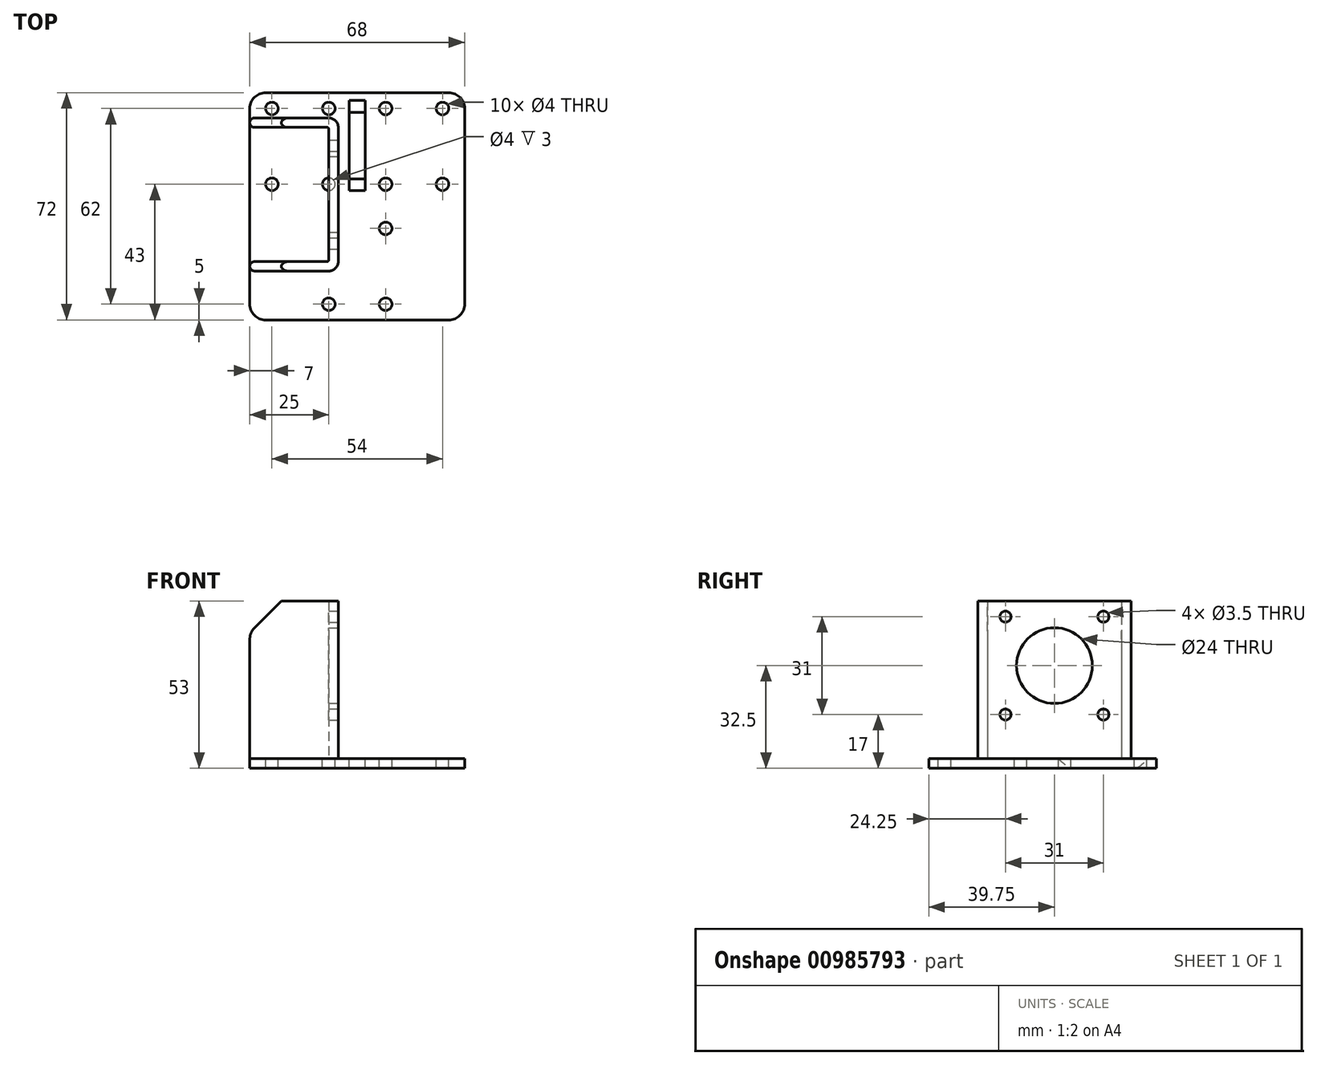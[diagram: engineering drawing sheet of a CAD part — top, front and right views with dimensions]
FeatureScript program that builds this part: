
annotation { "Feature Type Name" : "Feature", "Feature Type Description" : "" }
export const myFeature = defineFeature(function(context is Context, id is Id, definition is map)
    precondition{}
    {
        {
            var Q0;
            Q0=qCreatedBy(makeId("Top.planeOp"),FACE);
            var sketch = newSketch(context, id + "F0", { "sketchPlane" : qUnion([Q0])});
            skLineSegment(sketch, "E0.bottom", {"start": v(34, 0) * mm, "end": v(-34, 0) * mm});
            skLineSegment(sketch, "E0.top", {"start": v(34, 72) * mm, "end": v(-34, 72) * mm});
            skLineSegment(sketch, "E0.left", {"start": v(34, 0) * mm, "end": v(34, 72) * mm});
            skLineSegment(sketch, "E0.right", {"start": v(-34, 0) * mm, "end": v(-34, 72) * mm});
            skCircle(sketch, "E1", {"center": v(27, 67) * mm, "radius": 2 * mm});
            skCircle(sketch, "E2", {"center": v(27, 43) * mm, "radius": 2 * mm});
            skCircle(sketch, "E3", {"center": v(9, 67) * mm, "radius": 2 * mm});
            skCircle(sketch, "E4", {"center": v(9, 43) * mm, "radius": 2 * mm});
            skLineSegment(sketch, "E5", {"start": v(0, 72) * mm, "end": v(0, -67.13) * mm, "construction": true});
            skCircle(sketch, "E6.MirrorC", {"center": v(-27, 67) * mm, "radius": 2 * mm});
            skCircle(sketch, "E7.MirrorC", {"center": v(-27, 43) * mm, "radius": 2 * mm});
            skCircle(sketch, "E8.MirrorC", {"center": v(-9, 43) * mm, "radius": 2 * mm});
            skCircle(sketch, "E9.MirrorC", {"center": v(-9, 67) * mm, "radius": 2 * mm});
            skLineSegment(sketch, "E10", {"start": v(34, 36) * mm, "end": v(-10.03, 36) * mm, "construction": true});
            skCircle(sketch, "E11.MirrorC", {"center": v(9, 29) * mm, "radius": 2 * mm});
            skCircle(sketch, "E12.MirrorC", {"center": v(-9, 29) * mm, "radius": 2 * mm});
            skCircle(sketch, "E13.MirrorC", {"center": v(-9, 5) * mm, "radius": 2 * mm});
            skCircle(sketch, "E14.MirrorC", {"center": v(9, 5) * mm, "radius": 2 * mm});
            skLineSegment(sketch, "E15.bottom", {"start": v(3, 72) * mm, "end": v(33, 72) * mm, "construction": true});
            skLineSegment(sketch, "E15.top", {"start": v(3, 38) * mm, "end": v(33, 38) * mm, "construction": true});
            skLineSegment(sketch, "E15.left", {"start": v(3, 72) * mm, "end": v(3, 38) * mm, "construction": true});
            skLineSegment(sketch, "E15.right", {"start": v(33, 72) * mm, "end": v(33, 38) * mm, "construction": true});
            skLineSegment(sketch, "E16.bottom", {"start": v(15, 34) * mm, "end": v(-15, 34) * mm, "construction": true});
            skLineSegment(sketch, "E16.top", {"start": v(15, 0) * mm, "end": v(-15, 0) * mm, "construction": true});
            skLineSegment(sketch, "E16.left", {"start": v(15, 34) * mm, "end": v(15, 0) * mm, "construction": true});
            skLineSegment(sketch, "E16.right", {"start": v(-15, 34) * mm, "end": v(-15, 0) * mm, "construction": true});
            skLineSegment(sketch, "E17.MirrorCS", {"start": v(-3, 72) * mm, "end": v(-3, 38) * mm, "construction": true});
            skLineSegment(sketch, "E18.MirrorCS", {"start": v(-3, 38) * mm, "end": v(-33, 38) * mm, "construction": true});
            skLineSegment(sketch, "E19.MirrorCS", {"start": v(-33, 72) * mm, "end": v(-33, 38) * mm, "construction": true});
            skPoint(sketch, "E20", {"position": v(0, 0) * mm});
            skSolve(sketch);
        }
        {
            var Q0;
            Q0=makeQuery(id+"F0.imprint","IMPRINT",FACE,{"disambiguationData":[TD([[makeQuery(id+"F0.imprint","IMPRINT",EDGE,{"derivedFrom":sQuery(id+"F0.wireOp",EDGE,"E0.bottom")}),-1.0]])]});
            var Q1;
            Q1=makeQuery(id+"F0.imprint","IMPRINT",FACE,{"disambiguationData":[TD([[makeQuery(id+"F0.imprint","IMPRINT",EDGE,{"derivedFrom":sQuery(id+"F0.wireOp",EDGE,"E8.MirrorC")}),-1.0]])]});
            var Q2;
            Q2=makeQuery(id+"F0.imprint","IMPRINT",FACE,{"disambiguationData":[TD([[makeQuery(id+"F0.imprint","IMPRINT",EDGE,{"derivedFrom":sQuery(id+"F0.wireOp",EDGE,"E12.MirrorC")}),1.0]])]});
            extrude(context, id + "F1", {"entities" : qUnion([Q0, Q1, Q2]), "oppositeDirection" : true, "depth" : 3 * mm, "offsetDistance" : 25 * mm});
        }
        {
            var Q0;
            Q0=qCreatedBy(makeId("Top.planeOp"),FACE);
            var sketch = newSketch(context, id + "F2", { "sketchPlane" : qUnion([Q0])});
            skLineSegment(sketch, "E21.0", {"start": v(34, 72) * mm, "end": v(-34, 72) * mm});
            skLineSegment(sketch, "E22.0", {"start": v(34, 0) * mm, "end": v(34, 72) * mm});
            skLineSegment(sketch, "E23.0", {"start": v(34, 0) * mm, "end": v(-34, 0) * mm});
            skLineSegment(sketch, "E24.0", {"start": v(-34, 0) * mm, "end": v(-34, 72) * mm});
            skLineSegment(sketch, "E25", {"start": v(-34, 64) * mm, "end": v(-6, 64) * mm});
            skLineSegment(sketch, "E26", {"start": v(-6, 64) * mm, "end": v(-6, 15.5) * mm});
            skLineSegment(sketch, "E27", {"start": v(-6, 15.5) * mm, "end": v(-34, 15.5) * mm});
            skPoint(sketch, "E28", {"position": v(-6, 39.75) * mm});
            skPoint(sketch, "E29", {"position": v(-34, 36) * mm});
            skLineSegment(sketch, "E30.0", {"start": v(-9, 18.5) * mm, "end": v(-34, 18.5) * mm});
            skLineSegment(sketch, "E30.1", {"start": v(-9, 61) * mm, "end": v(-9, 18.5) * mm});
            skLineSegment(sketch, "E30.2", {"start": v(-34, 61) * mm, "end": v(-9, 61) * mm});
            skSolve(sketch);
        }
        {
            var Q0;
            {var subQ0=sQuery(id+"F2.wireOp",EDGE,"E25");Q0=makeQuery(id+"F2.imprint","IMPRINT",FACE,{"disambiguationData":[TD([[makeQuery(id+"F2.imprint","IMPRINT",EDGE,{"derivedFrom":subQ0}),-1.0]])]});}
            extrude(context, id + "F3", {"entities" : qUnion([Q0]), "operationType" : NewBodyOperationType.ADD, "depth" : 50 * mm, "offsetDistance" : 25 * mm});
        }
        {
            var Q0;
            {var subQ0=sQuery(id+"F2.wireOp",EDGE,"E24.0");Q0=makeQuery(id+"F3.opExtrude","CAP_EDGE",EDGE,{"disambiguationData":[OSD([subQ0]),TDD([makeQuery(id+"F2.imprint","IMPRINT",EDGE,{"disambiguationData":[TD([[makeQuery(id+"F2.imprint","INTERSECT",VERTEX,{"derivedFrom":[subQ0,sQuery(id+"F2.wireOp",EDGE,"E25")]}),1.0]])],"derivedFrom":subQ0})])],"isStart":false});}
            var Q1;
            {var subQ0=sQuery(id+"F2.wireOp",EDGE,"E24.0");Q1=makeQuery(id+"F3.opExtrude","CAP_EDGE",EDGE,{"disambiguationData":[OSD([subQ0]),TDD([makeQuery(id+"F2.imprint","IMPRINT",EDGE,{"disambiguationData":[TD([[makeQuery(id+"F2.imprint","INTERSECT",VERTEX,{"derivedFrom":[subQ0,sQuery(id+"F2.wireOp",EDGE,"E27")]}),-1.0]])],"derivedFrom":subQ0})])],"isStart":false});}
            chamfer(context, id + "F4", {"entities" : qUnion([Q0, Q1]), "width" : 10 * mm, "tangentPropagation" : true});
        }
        {
            var Q0;
            Q0=makeQuery(id+"F3.opExtrude","SWEPT_FACE",FACE,{"disambiguationData":[OSD([sQuery(id+"F2.wireOp",EDGE,"E26")])]});
            var sketch = newSketch(context, id + "F5", { "sketchPlane" : qUnion([Q0])});
            skPoint(sketch, "E31", {"position": v(74.45, 33.02) * mm});
            skPoint(sketch, "E32", {"position": v(29.84, 9.87) * mm});
            skSolve(sketch);
        }
        {
            var Q0;
            {var subQ0=sQuery(id+"F2.wireOp",EDGE,"E26");Q0=makeQuery(id+"F5.imprint","IMPRINT",FACE,{"disambiguationData":[TD([[makeQuery(id+"F5.imprint","IMPRINT",EDGE,{"derivedFrom":makeQuery(id+"F3.opExtrude","CAP_EDGE",EDGE,{"disambiguationData":[OSD([subQ0])],"isStart":false})}),1.0]])]});}
            var sketch = newSketch(context, id + "F6", { "sketchPlane" : qUnion([Q0])});
            skLineSegment(sketch, "E33.0.0", {"start": v(15.5, 0) * mm, "end": v(64, 0) * mm});
            skLineSegment(sketch, "E33.0.1", {"start": v(64, 0) * mm, "end": v(64, 50) * mm});
            skLineSegment(sketch, "E33.0.2", {"start": v(64, 50) * mm, "end": v(15.5, 50) * mm});
            skLineSegment(sketch, "E33.0.3", {"start": v(15.5, 50) * mm, "end": v(15.5, 0) * mm});
            skLineSegment(sketch, "E34", {"start": v(64, 50) * mm, "end": v(15.5, 0) * mm, "construction": true});
            skPoint(sketch, "E35", {"position": v(39.75, 25) * mm});
            skCircle(sketch, "E36", {"center": v(55.25, 45) * mm, "radius": 1.75 * mm});
            skCircle(sketch, "E37", {"center": v(55.25, 14) * mm, "radius": 1.75 * mm});
            skCircle(sketch, "E38", {"center": v(24.25, 45) * mm, "radius": 1.75 * mm});
            skCircle(sketch, "E39", {"center": v(24.25, 14) * mm, "radius": 1.75 * mm});
            skCircle(sketch, "E40", {"center": v(39.75, 29.5) * mm, "radius": 12 * mm});
            skSolve(sketch);
        }
        {
            var Q0;
            Q0=makeQuery(id+"F6.imprint","IMPRINT",FACE,{"disambiguationData":[TD([[makeQuery(id+"F6.imprint","IMPRINT",EDGE,{"derivedFrom":sQuery(id+"F6.wireOp",EDGE,"E36")}),1.0]])]});
            var Q1;
            Q1=makeQuery(id+"F6.imprint","IMPRINT",FACE,{"disambiguationData":[TD([[makeQuery(id+"F6.imprint","IMPRINT",EDGE,{"derivedFrom":sQuery(id+"F6.wireOp",EDGE,"E40")}),1.0]])]});
            var Q2;
            Q2=makeQuery(id+"F6.imprint","IMPRINT",FACE,{"disambiguationData":[TD([[makeQuery(id+"F6.imprint","IMPRINT",EDGE,{"derivedFrom":sQuery(id+"F6.wireOp",EDGE,"E37")}),1.0]])]});
            var Q3;
            Q3=makeQuery(id+"F6.imprint","IMPRINT",FACE,{"disambiguationData":[TD([[makeQuery(id+"F6.imprint","IMPRINT",EDGE,{"derivedFrom":sQuery(id+"F6.wireOp",EDGE,"E38")}),1.0]])]});
            var Q4;
            Q4=makeQuery(id+"F6.imprint","IMPRINT",FACE,{"disambiguationData":[TD([[makeQuery(id+"F6.imprint","IMPRINT",EDGE,{"derivedFrom":sQuery(id+"F6.wireOp",EDGE,"E39")}),1.0]])]});
            extrude(context, id + "F7", {"entities" : qUnion([Q0, Q1, Q2, Q3, Q4]), "operationType" : NewBodyOperationType.REMOVE, "oppositeDirection" : true, "depth" : 25 * mm, "offsetDistance" : 25 * mm});
        }
        {
            var Q0;
            Q0=makeQuery(id+"F1.opExtrude","SWEPT_EDGE",EDGE,{"disambiguationData":[OSD([sQuery(id+"F0.wireOp",EDGE,"E0.top"),sQuery(id+"F0.wireOp",EDGE,"E0.right")])]});
            var Q1;
            Q1=makeQuery(id+"F1.opExtrude","SWEPT_EDGE",EDGE,{"disambiguationData":[OSD([sQuery(id+"F0.wireOp",EDGE,"E0.top"),sQuery(id+"F0.wireOp",EDGE,"E0.left")])]});
            var Q2;
            Q2=makeQuery(id+"F1.opExtrude","SWEPT_EDGE",EDGE,{"disambiguationData":[OSD([sQuery(id+"F0.wireOp",EDGE,"E0.bottom"),sQuery(id+"F0.wireOp",EDGE,"E0.left")])]});
            var Q3;
            Q3=makeQuery(id+"F1.opExtrude","SWEPT_EDGE",EDGE,{"disambiguationData":[OSD([sQuery(id+"F0.wireOp",EDGE,"E0.bottom"),sQuery(id+"F0.wireOp",EDGE,"E0.right")])]});
            var Q4;
            {var subQ0=sQuery(id+"F2.wireOp",EDGE,"E24.0");var subQ1=makeQuery(id+"F2.imprint","IMPRINT",EDGE,{"disambiguationData":[TD([[makeQuery(id+"F2.imprint","INTERSECT",VERTEX,{"derivedFrom":[subQ0,sQuery(id+"F2.wireOp",EDGE,"E30.0")]}),1.0]])],"derivedFrom":subQ0});Q4=makeQuery(id+"F4.opChamfer","BLEND_EDGE",EDGE,{"blendedFrom":[makeQuery(id+"F3.opExtrude","CAP_EDGE",EDGE,{"disambiguationData":[OSD([subQ0]),TDD([subQ1])],"isStart":false}),makeQuery(id+"F3.boolean.opBoolean","MERGE",FACE,{"derivedFrom":[makeQuery(id+"F1.opExtrude","SWEPT_FACE",FACE,{"disambiguationData":[OSD([sQuery(id+"F0.wireOp",EDGE,"E0.right")])]}),makeQuery(id+"F3.opExtrude","SWEPT_FACE",FACE,{"disambiguationData":[OSD([subQ0]),TDD([makeQuery(id+"F2.imprint","IMPRINT",EDGE,{"disambiguationData":[TD([[makeQuery(id+"F2.imprint","INTERSECT",VERTEX,{"derivedFrom":[subQ0,sQuery(id+"F2.wireOp",EDGE,"E25")]}),1.0]])],"derivedFrom":subQ0})])]}),makeQuery(id+"F3.opExtrude","SWEPT_FACE",FACE,{"disambiguationData":[OSD([subQ0]),TDD([subQ1])]})]})],"blendedInto":[makeQuery(id+"F3.boolean.opBoolean","MERGE",FACE,{"derivedFrom":[makeQuery(id+"F1.opExtrude","SWEPT_FACE",FACE,{"disambiguationData":[OSD([sQuery(id+"F0.wireOp",EDGE,"E0.right")])]}),makeQuery(id+"F3.opExtrude","SWEPT_FACE",FACE,{"disambiguationData":[OSD([subQ0]),TDD([makeQuery(id+"F2.imprint","IMPRINT",EDGE,{"disambiguationData":[TD([[makeQuery(id+"F2.imprint","INTERSECT",VERTEX,{"derivedFrom":[subQ0,sQuery(id+"F2.wireOp",EDGE,"E25")]}),1.0]])],"derivedFrom":subQ0})])]}),makeQuery(id+"F3.opExtrude","SWEPT_FACE",FACE,{"disambiguationData":[OSD([subQ0]),TDD([subQ1])]})]})]});}
            var Q5;
            {var subQ0=sQuery(id+"F2.wireOp",EDGE,"E24.0");var subQ1=makeQuery(id+"F2.imprint","IMPRINT",EDGE,{"disambiguationData":[TD([[makeQuery(id+"F2.imprint","INTERSECT",VERTEX,{"derivedFrom":[subQ0,sQuery(id+"F2.wireOp",EDGE,"E25")]}),1.0]])],"derivedFrom":subQ0});Q5=makeQuery(id+"F4.opChamfer","BLEND_EDGE",EDGE,{"blendedFrom":[makeQuery(id+"F3.opExtrude","CAP_EDGE",EDGE,{"disambiguationData":[OSD([subQ0]),TDD([subQ1])],"isStart":false}),makeQuery(id+"F3.boolean.opBoolean","MERGE",FACE,{"derivedFrom":[makeQuery(id+"F1.opExtrude","SWEPT_FACE",FACE,{"disambiguationData":[OSD([sQuery(id+"F0.wireOp",EDGE,"E0.right")])]}),makeQuery(id+"F3.opExtrude","SWEPT_FACE",FACE,{"disambiguationData":[OSD([subQ0]),TDD([subQ1])]}),makeQuery(id+"F3.opExtrude","SWEPT_FACE",FACE,{"disambiguationData":[OSD([subQ0]),TDD([makeQuery(id+"F2.imprint","IMPRINT",EDGE,{"disambiguationData":[TD([[makeQuery(id+"F2.imprint","INTERSECT",VERTEX,{"derivedFrom":[subQ0,sQuery(id+"F2.wireOp",EDGE,"E30.0")]}),1.0]])],"derivedFrom":subQ0})])]})]})],"blendedInto":[makeQuery(id+"F3.boolean.opBoolean","MERGE",FACE,{"derivedFrom":[makeQuery(id+"F1.opExtrude","SWEPT_FACE",FACE,{"disambiguationData":[OSD([sQuery(id+"F0.wireOp",EDGE,"E0.right")])]}),makeQuery(id+"F3.opExtrude","SWEPT_FACE",FACE,{"disambiguationData":[OSD([subQ0]),TDD([subQ1])]}),makeQuery(id+"F3.opExtrude","SWEPT_FACE",FACE,{"disambiguationData":[OSD([subQ0]),TDD([makeQuery(id+"F2.imprint","IMPRINT",EDGE,{"disambiguationData":[TD([[makeQuery(id+"F2.imprint","INTERSECT",VERTEX,{"derivedFrom":[subQ0,sQuery(id+"F2.wireOp",EDGE,"E30.0")]}),1.0]])],"derivedFrom":subQ0})])]})]})]});}
            fillet(context, id + "F8", {"entities" : qUnion([Q0, Q1, Q2, Q3, Q4, Q5]), "tangentPropagation" : true, "radius" : 5 * mm, "defaultsChanged" : true, "vertexSettings" : [], "allowEdgeOverflow" : false});
        }
        {
            var Q0;
            Q0=makeQuery(id+"F3.opExtrude","SWEPT_EDGE",EDGE,{"disambiguationData":[OSD([sQuery(id+"F2.wireOp",EDGE,"E24.0"),sQuery(id+"F2.wireOp",EDGE,"E25")])]});
            var Q1;
            Q1=makeQuery(id+"F3.opExtrude","SWEPT_EDGE",EDGE,{"disambiguationData":[OSD([sQuery(id+"F2.wireOp",EDGE,"E24.0"),sQuery(id+"F2.wireOp",EDGE,"E30.2")])]});
            var Q2;
            {var subQ0=sQuery(id+"F2.wireOp",EDGE,"E27");var subQ1=sQuery(id+"F2.wireOp",EDGE,"E24.0");Q2=makeQuery(id+"F4.opChamfer","BLEND_EDGE",EDGE,{"blendedFrom":[makeQuery(id+"F3.opExtrude","CAP_EDGE",EDGE,{"disambiguationData":[OSD([subQ1]),TDD([makeQuery(id+"F2.imprint","IMPRINT",EDGE,{"disambiguationData":[TD([[makeQuery(id+"F2.imprint","INTERSECT",VERTEX,{"derivedFrom":[subQ1,sQuery(id+"F2.wireOp",EDGE,"E30.0")]}),1.0]])],"derivedFrom":subQ1})])],"isStart":false}),makeQuery(id+"F3.opExtrude","SWEPT_FACE",FACE,{"disambiguationData":[OSD([subQ0])]})],"blendedInto":[makeQuery(id+"F3.opExtrude","SWEPT_FACE",FACE,{"disambiguationData":[OSD([subQ0])]})]});}
            var Q3;
            {var subQ0=sQuery(id+"F2.wireOp",EDGE,"E30.0");var subQ1=sQuery(id+"F2.wireOp",EDGE,"E24.0");Q3=makeQuery(id+"F4.opChamfer","BLEND_EDGE",EDGE,{"blendedFrom":[makeQuery(id+"F3.opExtrude","CAP_EDGE",EDGE,{"disambiguationData":[OSD([subQ1]),TDD([makeQuery(id+"F2.imprint","IMPRINT",EDGE,{"disambiguationData":[TD([[makeQuery(id+"F2.imprint","INTERSECT",VERTEX,{"derivedFrom":[subQ1,subQ0]}),1.0]])],"derivedFrom":subQ1})])],"isStart":false}),makeQuery(id+"F3.opExtrude","SWEPT_FACE",FACE,{"disambiguationData":[OSD([subQ0])]})],"blendedInto":[makeQuery(id+"F3.opExtrude","SWEPT_FACE",FACE,{"disambiguationData":[OSD([subQ0])]})]});}
            var Q4;
            {var subQ0=sQuery(id+"F2.wireOp",EDGE,"E27");var subQ1=sQuery(id+"F2.wireOp",EDGE,"E24.0");var subQ2=makeQuery(id+"F2.imprint","IMPRINT",EDGE,{"disambiguationData":[TD([[makeQuery(id+"F2.imprint","INTERSECT",VERTEX,{"derivedFrom":[subQ1,sQuery(id+"F2.wireOp",EDGE,"E30.0")]}),1.0]])],"derivedFrom":subQ1});Q4=makeQuery(id+"F8.opFillet","BLEND_EDGE",EDGE,{"blendedFrom":[makeQuery(id+"F4.opChamfer","BLEND_EDGE",EDGE,{"blendedFrom":[makeQuery(id+"F3.opExtrude","CAP_EDGE",EDGE,{"disambiguationData":[OSD([subQ1]),TDD([subQ2])],"isStart":false}),makeQuery(id+"F3.boolean.opBoolean","MERGE",FACE,{"derivedFrom":[makeQuery(id+"F1.opExtrude","SWEPT_FACE",FACE,{"disambiguationData":[OSD([sQuery(id+"F0.wireOp",EDGE,"E0.right")])]}),makeQuery(id+"F3.opExtrude","SWEPT_FACE",FACE,{"disambiguationData":[OSD([subQ1]),TDD([makeQuery(id+"F2.imprint","IMPRINT",EDGE,{"disambiguationData":[TD([[makeQuery(id+"F2.imprint","INTERSECT",VERTEX,{"derivedFrom":[subQ1,sQuery(id+"F2.wireOp",EDGE,"E25")]}),1.0]])],"derivedFrom":subQ1})])]}),makeQuery(id+"F3.opExtrude","SWEPT_FACE",FACE,{"disambiguationData":[OSD([subQ1]),TDD([subQ2])]})]})],"blendedInto":[makeQuery(id+"F3.boolean.opBoolean","MERGE",FACE,{"derivedFrom":[makeQuery(id+"F1.opExtrude","SWEPT_FACE",FACE,{"disambiguationData":[OSD([sQuery(id+"F0.wireOp",EDGE,"E0.right")])]}),makeQuery(id+"F3.opExtrude","SWEPT_FACE",FACE,{"disambiguationData":[OSD([subQ1]),TDD([makeQuery(id+"F2.imprint","IMPRINT",EDGE,{"disambiguationData":[TD([[makeQuery(id+"F2.imprint","INTERSECT",VERTEX,{"derivedFrom":[subQ1,sQuery(id+"F2.wireOp",EDGE,"E25")]}),1.0]])],"derivedFrom":subQ1})])]}),makeQuery(id+"F3.opExtrude","SWEPT_FACE",FACE,{"disambiguationData":[OSD([subQ1]),TDD([subQ2])]})]})]}),makeQuery(id+"F3.opExtrude","SWEPT_FACE",FACE,{"disambiguationData":[OSD([subQ0])]})],"blendedInto":[makeQuery(id+"F3.opExtrude","SWEPT_FACE",FACE,{"disambiguationData":[OSD([subQ0])]})]});}
            var Q5;
            Q5=makeQuery(id+"F3.opExtrude","SWEPT_EDGE",EDGE,{"disambiguationData":[OSD([sQuery(id+"F2.wireOp",EDGE,"E24.0"),sQuery(id+"F2.wireOp",EDGE,"E27")])]});
            var Q6;
            Q6=makeQuery(id+"F3.opExtrude","SWEPT_EDGE",EDGE,{"disambiguationData":[OSD([sQuery(id+"F2.wireOp",EDGE,"E24.0"),sQuery(id+"F2.wireOp",EDGE,"E30.0")])]});
            var Q7;
            {var subQ0=sQuery(id+"F2.wireOp",EDGE,"E30.0");var subQ1=sQuery(id+"F2.wireOp",EDGE,"E24.0");var subQ2=makeQuery(id+"F2.imprint","IMPRINT",EDGE,{"disambiguationData":[TD([[makeQuery(id+"F2.imprint","INTERSECT",VERTEX,{"derivedFrom":[subQ1,subQ0]}),1.0]])],"derivedFrom":subQ1});Q7=makeQuery(id+"F8.opFillet","BLEND_EDGE",EDGE,{"blendedFrom":[makeQuery(id+"F4.opChamfer","BLEND_EDGE",EDGE,{"blendedFrom":[makeQuery(id+"F3.opExtrude","CAP_EDGE",EDGE,{"disambiguationData":[OSD([subQ1]),TDD([subQ2])],"isStart":false}),makeQuery(id+"F3.boolean.opBoolean","MERGE",FACE,{"derivedFrom":[makeQuery(id+"F1.opExtrude","SWEPT_FACE",FACE,{"disambiguationData":[OSD([sQuery(id+"F0.wireOp",EDGE,"E0.right")])]}),makeQuery(id+"F3.opExtrude","SWEPT_FACE",FACE,{"disambiguationData":[OSD([subQ1]),TDD([makeQuery(id+"F2.imprint","IMPRINT",EDGE,{"disambiguationData":[TD([[makeQuery(id+"F2.imprint","INTERSECT",VERTEX,{"derivedFrom":[subQ1,sQuery(id+"F2.wireOp",EDGE,"E25")]}),1.0]])],"derivedFrom":subQ1})])]}),makeQuery(id+"F3.opExtrude","SWEPT_FACE",FACE,{"disambiguationData":[OSD([subQ1]),TDD([subQ2])]})]})],"blendedInto":[makeQuery(id+"F3.boolean.opBoolean","MERGE",FACE,{"derivedFrom":[makeQuery(id+"F1.opExtrude","SWEPT_FACE",FACE,{"disambiguationData":[OSD([sQuery(id+"F0.wireOp",EDGE,"E0.right")])]}),makeQuery(id+"F3.opExtrude","SWEPT_FACE",FACE,{"disambiguationData":[OSD([subQ1]),TDD([makeQuery(id+"F2.imprint","IMPRINT",EDGE,{"disambiguationData":[TD([[makeQuery(id+"F2.imprint","INTERSECT",VERTEX,{"derivedFrom":[subQ1,sQuery(id+"F2.wireOp",EDGE,"E25")]}),1.0]])],"derivedFrom":subQ1})])]}),makeQuery(id+"F3.opExtrude","SWEPT_FACE",FACE,{"disambiguationData":[OSD([subQ1]),TDD([subQ2])]})]})]}),makeQuery(id+"F3.opExtrude","SWEPT_FACE",FACE,{"disambiguationData":[OSD([subQ0])]})],"blendedInto":[makeQuery(id+"F3.opExtrude","SWEPT_FACE",FACE,{"disambiguationData":[OSD([subQ0])]})]});}
            var Q8;
            {var subQ0=sQuery(id+"F2.wireOp",EDGE,"E25");var subQ1=sQuery(id+"F2.wireOp",EDGE,"E24.0");var subQ2=makeQuery(id+"F2.imprint","IMPRINT",EDGE,{"disambiguationData":[TD([[makeQuery(id+"F2.imprint","INTERSECT",VERTEX,{"derivedFrom":[subQ1,subQ0]}),1.0]])],"derivedFrom":subQ1});Q8=makeQuery(id+"F8.opFillet","BLEND_EDGE",EDGE,{"blendedFrom":[makeQuery(id+"F4.opChamfer","BLEND_EDGE",EDGE,{"blendedFrom":[makeQuery(id+"F3.opExtrude","CAP_EDGE",EDGE,{"disambiguationData":[OSD([subQ1]),TDD([subQ2])],"isStart":false}),makeQuery(id+"F3.boolean.opBoolean","MERGE",FACE,{"derivedFrom":[makeQuery(id+"F1.opExtrude","SWEPT_FACE",FACE,{"disambiguationData":[OSD([sQuery(id+"F0.wireOp",EDGE,"E0.right")])]}),makeQuery(id+"F3.opExtrude","SWEPT_FACE",FACE,{"disambiguationData":[OSD([subQ1]),TDD([subQ2])]}),makeQuery(id+"F3.opExtrude","SWEPT_FACE",FACE,{"disambiguationData":[OSD([subQ1]),TDD([makeQuery(id+"F2.imprint","IMPRINT",EDGE,{"disambiguationData":[TD([[makeQuery(id+"F2.imprint","INTERSECT",VERTEX,{"derivedFrom":[subQ1,sQuery(id+"F2.wireOp",EDGE,"E30.0")]}),1.0]])],"derivedFrom":subQ1})])]})]})],"blendedInto":[makeQuery(id+"F3.boolean.opBoolean","MERGE",FACE,{"derivedFrom":[makeQuery(id+"F1.opExtrude","SWEPT_FACE",FACE,{"disambiguationData":[OSD([sQuery(id+"F0.wireOp",EDGE,"E0.right")])]}),makeQuery(id+"F3.opExtrude","SWEPT_FACE",FACE,{"disambiguationData":[OSD([subQ1]),TDD([subQ2])]}),makeQuery(id+"F3.opExtrude","SWEPT_FACE",FACE,{"disambiguationData":[OSD([subQ1]),TDD([makeQuery(id+"F2.imprint","IMPRINT",EDGE,{"disambiguationData":[TD([[makeQuery(id+"F2.imprint","INTERSECT",VERTEX,{"derivedFrom":[subQ1,sQuery(id+"F2.wireOp",EDGE,"E30.0")]}),1.0]])],"derivedFrom":subQ1})])]})]})]}),makeQuery(id+"F3.opExtrude","SWEPT_FACE",FACE,{"disambiguationData":[OSD([subQ0])]})],"blendedInto":[makeQuery(id+"F3.opExtrude","SWEPT_FACE",FACE,{"disambiguationData":[OSD([subQ0])]})]});}
            var Q9;
            {var subQ0=sQuery(id+"F2.wireOp",EDGE,"E30.2");var subQ1=sQuery(id+"F2.wireOp",EDGE,"E24.0");var subQ2=makeQuery(id+"F2.imprint","IMPRINT",EDGE,{"disambiguationData":[TD([[makeQuery(id+"F2.imprint","INTERSECT",VERTEX,{"derivedFrom":[subQ1,sQuery(id+"F2.wireOp",EDGE,"E25")]}),1.0]])],"derivedFrom":subQ1});Q9=makeQuery(id+"F8.opFillet","BLEND_EDGE",EDGE,{"blendedFrom":[makeQuery(id+"F4.opChamfer","BLEND_EDGE",EDGE,{"blendedFrom":[makeQuery(id+"F3.opExtrude","CAP_EDGE",EDGE,{"disambiguationData":[OSD([subQ1]),TDD([subQ2])],"isStart":false}),makeQuery(id+"F3.boolean.opBoolean","MERGE",FACE,{"derivedFrom":[makeQuery(id+"F1.opExtrude","SWEPT_FACE",FACE,{"disambiguationData":[OSD([sQuery(id+"F0.wireOp",EDGE,"E0.right")])]}),makeQuery(id+"F3.opExtrude","SWEPT_FACE",FACE,{"disambiguationData":[OSD([subQ1]),TDD([subQ2])]}),makeQuery(id+"F3.opExtrude","SWEPT_FACE",FACE,{"disambiguationData":[OSD([subQ1]),TDD([makeQuery(id+"F2.imprint","IMPRINT",EDGE,{"disambiguationData":[TD([[makeQuery(id+"F2.imprint","INTERSECT",VERTEX,{"derivedFrom":[subQ1,sQuery(id+"F2.wireOp",EDGE,"E30.0")]}),1.0]])],"derivedFrom":subQ1})])]})]})],"blendedInto":[makeQuery(id+"F3.boolean.opBoolean","MERGE",FACE,{"derivedFrom":[makeQuery(id+"F1.opExtrude","SWEPT_FACE",FACE,{"disambiguationData":[OSD([sQuery(id+"F0.wireOp",EDGE,"E0.right")])]}),makeQuery(id+"F3.opExtrude","SWEPT_FACE",FACE,{"disambiguationData":[OSD([subQ1]),TDD([subQ2])]}),makeQuery(id+"F3.opExtrude","SWEPT_FACE",FACE,{"disambiguationData":[OSD([subQ1]),TDD([makeQuery(id+"F2.imprint","IMPRINT",EDGE,{"disambiguationData":[TD([[makeQuery(id+"F2.imprint","INTERSECT",VERTEX,{"derivedFrom":[subQ1,sQuery(id+"F2.wireOp",EDGE,"E30.0")]}),1.0]])],"derivedFrom":subQ1})])]})]})]}),makeQuery(id+"F3.opExtrude","SWEPT_FACE",FACE,{"disambiguationData":[OSD([subQ0])]})],"blendedInto":[makeQuery(id+"F3.opExtrude","SWEPT_FACE",FACE,{"disambiguationData":[OSD([subQ0])]})]});}
            var Q10;
            {var subQ0=sQuery(id+"F2.wireOp",EDGE,"E30.2");var subQ1=sQuery(id+"F2.wireOp",EDGE,"E24.0");Q10=makeQuery(id+"F4.opChamfer","BLEND_EDGE",EDGE,{"blendedFrom":[makeQuery(id+"F3.opExtrude","CAP_EDGE",EDGE,{"disambiguationData":[OSD([subQ1]),TDD([makeQuery(id+"F2.imprint","IMPRINT",EDGE,{"disambiguationData":[TD([[makeQuery(id+"F2.imprint","INTERSECT",VERTEX,{"derivedFrom":[subQ1,sQuery(id+"F2.wireOp",EDGE,"E25")]}),1.0]])],"derivedFrom":subQ1})])],"isStart":false}),makeQuery(id+"F3.opExtrude","SWEPT_FACE",FACE,{"disambiguationData":[OSD([subQ0])]})],"blendedInto":[makeQuery(id+"F3.opExtrude","SWEPT_FACE",FACE,{"disambiguationData":[OSD([subQ0])]})]});}
            var Q11;
            {var subQ0=sQuery(id+"F2.wireOp",EDGE,"E25");var subQ1=sQuery(id+"F2.wireOp",EDGE,"E24.0");Q11=makeQuery(id+"F4.opChamfer","BLEND_EDGE",EDGE,{"blendedFrom":[makeQuery(id+"F3.opExtrude","CAP_EDGE",EDGE,{"disambiguationData":[OSD([subQ1]),TDD([makeQuery(id+"F2.imprint","IMPRINT",EDGE,{"disambiguationData":[TD([[makeQuery(id+"F2.imprint","INTERSECT",VERTEX,{"derivedFrom":[subQ1,subQ0]}),1.0]])],"derivedFrom":subQ1})])],"isStart":false}),makeQuery(id+"F3.opExtrude","SWEPT_FACE",FACE,{"disambiguationData":[OSD([subQ0])]})],"blendedInto":[makeQuery(id+"F3.opExtrude","SWEPT_FACE",FACE,{"disambiguationData":[OSD([subQ0])]})]});}
            fillet(context, id + "F9", {"entities" : qUnion([Q0, Q1, Q2, Q3, Q4, Q5, Q6, Q7, Q8, Q9, Q10, Q11]), "tangentPropagation" : true, "radius" : 1.5 * mm, "defaultsChanged" : true, "vertexSettings" : [], "allowEdgeOverflow" : false});
        }
        {
            var Q0;
            Q0=makeQuery(id+"F3.opExtrude","SWEPT_EDGE",EDGE,{"disambiguationData":[OSD([sQuery(id+"F2.wireOp",EDGE,"E26"),sQuery(id+"F2.wireOp",EDGE,"E27")])]});
            var Q1;
            Q1=makeQuery(id+"F3.opExtrude","SWEPT_EDGE",EDGE,{"disambiguationData":[OSD([sQuery(id+"F2.wireOp",EDGE,"E25"),sQuery(id+"F2.wireOp",EDGE,"E26")])]});
            fillet(context, id + "F10", {"entities" : qUnion([Q0, Q1]), "tangentPropagation" : true, "radius" : 3 * mm, "defaultsChanged" : true, "vertexSettings" : [], "allowEdgeOverflow" : false});
        }
        {
            var Q0;
            Q0=makeQuery(id+"F3.opExtrude","SWEPT_EDGE",EDGE,{"disambiguationData":[OSD([sQuery(id+"F2.wireOp",EDGE,"E30.0"),sQuery(id+"F2.wireOp",EDGE,"E30.1")])]});
            var Q1;
            Q1=makeQuery(id+"F3.opExtrude","SWEPT_EDGE",EDGE,{"disambiguationData":[OSD([sQuery(id+"F2.wireOp",EDGE,"E30.1"),sQuery(id+"F2.wireOp",EDGE,"E30.2")])]});
            fillet(context, id + "F11", {"entities" : qUnion([Q0, Q1]), "tangentPropagation" : true, "radius" : .5 * mm, "defaultsChanged" : true, "vertexSettings" : [], "allowEdgeOverflow" : false});
        }
        {
            var Q0;
            Q0=makeQuery(id+"F3.opExtrude","SWEPT_FACE",FACE,{"disambiguationData":[OSD([sQuery(id+"F2.wireOp",EDGE,"E26")])]});
            cPlane(context, id + "F12", {"entities" : qUnion([Q0]), "cplaneType" : CPlaneType.OFFSET, "offset" : 6 * mm, "width" : 150 * mm, "height" : 150 * mm});
        }
        {
            var Q0;
            Q0=qCreatedBy(id+"F12.planeOp",FACE);
            var sketch = newSketch(context, id + "F13", { "sketchPlane" : qUnion([Q0])});
            skCircle(sketch, "E41.0", {"center": v(55.25, 14) * mm, "radius": 1.75 * mm});
            skCircle(sketch, "E42", {"center": v(55.25, 14) * mm, "radius": 20 * mm});
            skSolve(sketch);
        }
        {
            var Q0;
            Q0=makeQuery(id+"F13.imprint","IMPRINT",FACE,{"disambiguationData":[TD([[makeQuery(id+"F13.imprint","IMPRINT",EDGE,{"derivedFrom":sQuery(id+"F13.wireOp",EDGE,"E41.0")}),-1.0]])]});
            extrude(context, id + "F14", {"entities" : qUnion([Q0]), "operationType" : NewBodyOperationType.REMOVE, "endBound" : BoundingType.SYMMETRIC, "depth" : 5 * mm, "offsetDistance" : 25 * mm});
        }
    });
